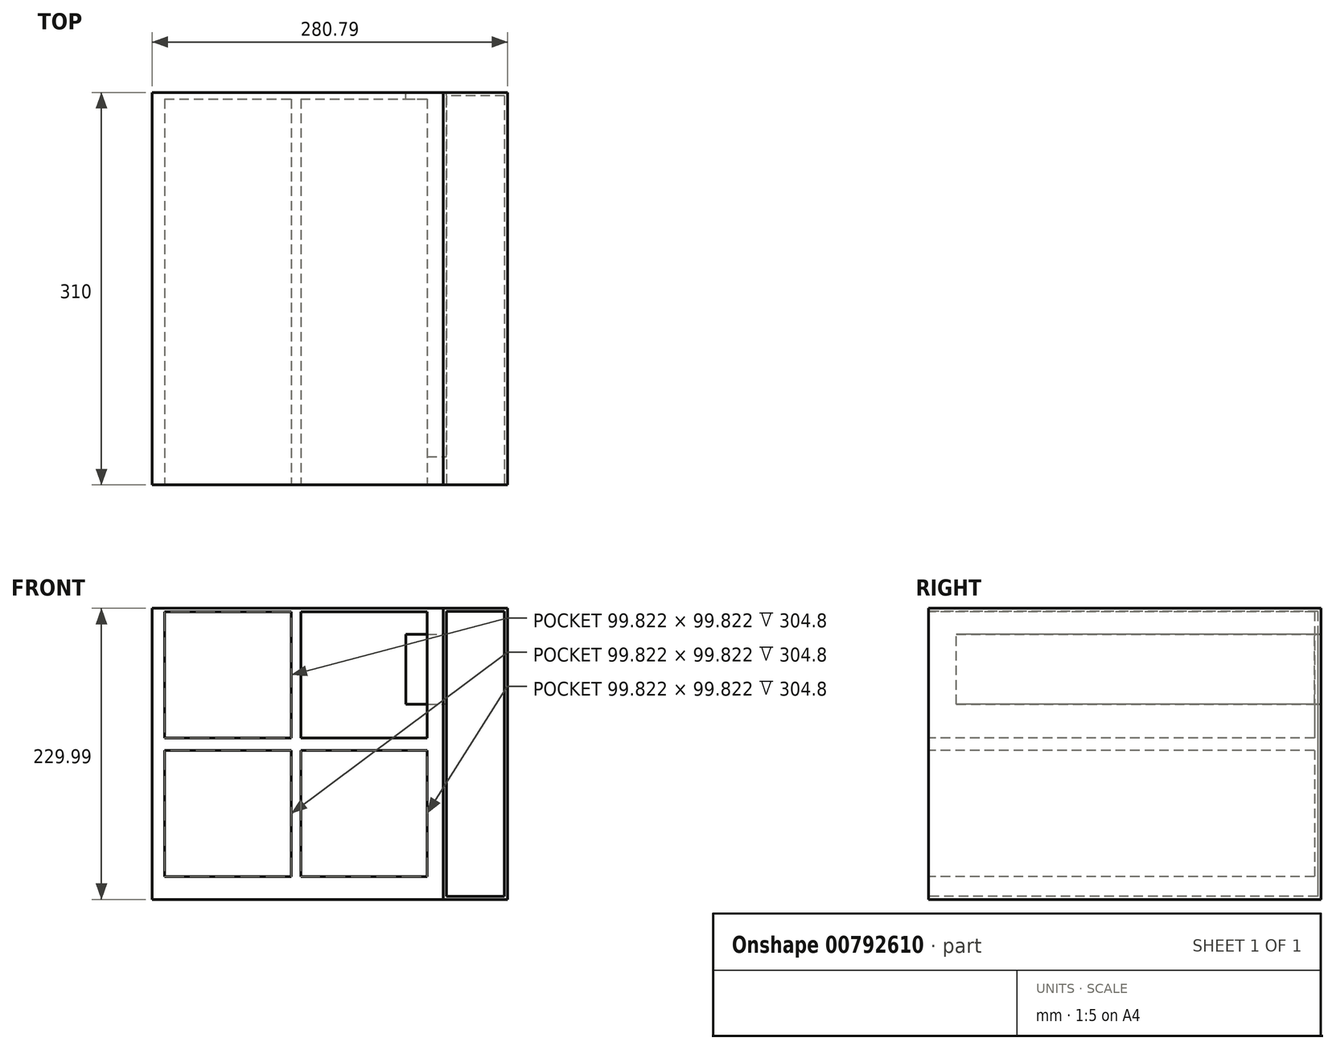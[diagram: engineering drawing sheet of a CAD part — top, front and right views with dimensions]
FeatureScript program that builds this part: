
annotation { "Feature Type Name" : "Feature", "Feature Type Description" : "" }
export const myFeature = defineFeature(function(context is Context, id is Id, definition is map)
    precondition{}
    {
        {
            var Q0;
            Q0=qCreatedBy(makeId("Front.planeOp"),FACE);
            var sketch = newSketch(context, id + "F0", { "sketchPlane" : qUnion([Q0])});
            skLineSegment(sketch, "E0.bottom", {"start": v(-110.85, 155.14) * mm, "end": v(119.14, 155.14) * mm});
            skLineSegment(sketch, "E0.top", {"start": v(-110.85, -74.85) * mm, "end": v(119.14, -74.85) * mm});
            skLineSegment(sketch, "E0.left", {"start": v(-110.85, 155.14) * mm, "end": v(-110.85, -74.85) * mm});
            skLineSegment(sketch, "E0.right", {"start": v(119.14, 155.14) * mm, "end": v(119.14, -74.85) * mm});
            skSolve(sketch);
        }
        {
            var Q0;
            Q0 = qSketchRegion(id + "F0", true);
            extrude(context, id + "F1", {"entities" : qUnion([Q0]), "oppositeDirection" : true, "depth" : 310 * mm, "offsetDistance" : 25.4 * mm});
        }
        {
            var Q0;
            Q0=makeQuery(id+"F1.opExtrude","CAP_FACE",FACE,{"disambiguationData":[OSD([sQuery(id+"F0.wireOp",EDGE,"E0.bottom"),sQuery(id+"F0.wireOp",EDGE,"E0.top"),sQuery(id+"F0.wireOp",EDGE,"E0.left"),sQuery(id+"F0.wireOp",EDGE,"E0.right")])],"isStart":true});
            var sketch = newSketch(context, id + "F2", { "sketchPlane" : qUnion([Q0])});
            skLineSegment(sketch, "E1", {"start": v(-110.85, 127.91) * mm, "end": v(-100.87, 127.91) * mm});
            skLineSegment(sketch, "E2.bottom", {"start": v(-100.87, 152.43) * mm, "end": v(-1.05, 152.43) * mm});
            skLineSegment(sketch, "E2.top", {"start": v(-100.87, 52.6) * mm, "end": v(-1.05, 52.6) * mm});
            skLineSegment(sketch, "E2.left", {"start": v(-100.87, 152.43) * mm, "end": v(-100.87, 52.6) * mm});
            skLineSegment(sketch, "E2.right", {"start": v(-1.05, 152.43) * mm, "end": v(-1.05, 52.6) * mm});
            skSolve(sketch);
        }
        {
            var Q0;
            {var subQ3=sQuery(id+"F2.wireOp",EDGE,"E2.bottom");Q0=makeQuery(id+"F2.imprint","IMPRINT",FACE,{"disambiguationData":[TD([[makeQuery(id+"F2.imprint","IMPRINT",EDGE,{"derivedFrom":subQ3}),-1.0]])]});}
            extrude(context, id + "F3", {"entities" : qUnion([Q0]), "operationType" : NewBodyOperationType.REMOVE, "oppositeDirection" : true, "depth" : 304.8 * mm, "offsetDistance" : 25.4 * mm});
        }
        {
            var Q0;
            Q0=makeQuery(id+"F1.opExtrude","CAP_FACE",FACE,{"disambiguationData":[OSD([sQuery(id+"F0.wireOp",EDGE,"E0.bottom"),sQuery(id+"F0.wireOp",EDGE,"E0.top"),sQuery(id+"F0.wireOp",EDGE,"E0.left"),sQuery(id+"F0.wireOp",EDGE,"E0.right")])],"isStart":true});
            var sketch = newSketch(context, id + "F4", { "sketchPlane" : qUnion([Q0])});
            skLineSegment(sketch, "E3.bottom", {"start": v(6.52, 152.43) * mm, "end": v(106.34, 152.43) * mm});
            skLineSegment(sketch, "E3.top", {"start": v(6.52, 52.6) * mm, "end": v(106.34, 52.6) * mm});
            skLineSegment(sketch, "E3.left", {"start": v(6.52, 152.43) * mm, "end": v(6.52, 52.6) * mm});
            skLineSegment(sketch, "E3.right", {"start": v(106.34, 152.43) * mm, "end": v(106.34, 52.6) * mm});
            skSolve(sketch);
        }
        {
            var Q0;
            Q0=makeQuery(id+"F4.imprint","IMPRINT",FACE,{"disambiguationData":[TD([[makeQuery(id+"F4.imprint","IMPRINT",EDGE,{"derivedFrom":sQuery(id+"F4.wireOp",EDGE,"E3.bottom")}),-1.0]])]});
            extrude(context, id + "F5", {"entities" : qUnion([Q0]), "operationType" : NewBodyOperationType.REMOVE, "oppositeDirection" : true, "depth" : 304.8 * mm, "offsetDistance" : 25.4 * mm});
        }
        {
            var Q0;
            Q0=makeQuery(id+"F1.opExtrude","CAP_FACE",FACE,{"disambiguationData":[OSD([sQuery(id+"F0.wireOp",EDGE,"E0.bottom"),sQuery(id+"F0.wireOp",EDGE,"E0.top"),sQuery(id+"F0.wireOp",EDGE,"E0.left"),sQuery(id+"F0.wireOp",EDGE,"E0.right")])],"isStart":true});
            var sketch = newSketch(context, id + "F6", { "sketchPlane" : qUnion([Q0])});
            skLineSegment(sketch, "E4.bottom", {"start": v(-100.87, 42.92) * mm, "end": v(-1.05, 42.92) * mm});
            skLineSegment(sketch, "E4.top", {"start": v(-100.87, -56.9) * mm, "end": v(-1.05, -56.9) * mm});
            skLineSegment(sketch, "E4.left", {"start": v(-100.87, 42.92) * mm, "end": v(-100.87, -56.9) * mm});
            skLineSegment(sketch, "E4.right", {"start": v(-1.05, 42.92) * mm, "end": v(-1.05, -56.9) * mm});
            skSolve(sketch);
        }
        {
            var Q0;
            Q0 = qSketchRegion(id + "F6", true);
            extrude(context, id + "F7", {"entities" : qUnion([Q0]), "operationType" : NewBodyOperationType.REMOVE, "oppositeDirection" : true, "depth" : 304.8 * mm, "offsetDistance" : 25.4 * mm});
        }
        {
            var Q0;
            Q0=makeQuery(id+"F1.opExtrude","CAP_FACE",FACE,{"disambiguationData":[OSD([sQuery(id+"F0.wireOp",EDGE,"E0.bottom"),sQuery(id+"F0.wireOp",EDGE,"E0.top"),sQuery(id+"F0.wireOp",EDGE,"E0.left"),sQuery(id+"F0.wireOp",EDGE,"E0.right")])],"isStart":true});
            var sketch = newSketch(context, id + "F8", { "sketchPlane" : qUnion([Q0])});
            skLineSegment(sketch, "E5.bottom", {"start": v(6.52, 42.92) * mm, "end": v(106.34, 42.92) * mm});
            skLineSegment(sketch, "E5.top", {"start": v(6.52, -56.9) * mm, "end": v(106.34, -56.9) * mm});
            skLineSegment(sketch, "E5.left", {"start": v(6.52, 42.92) * mm, "end": v(6.52, -56.9) * mm});
            skLineSegment(sketch, "E5.right", {"start": v(106.34, 42.92) * mm, "end": v(106.34, -56.9) * mm});
            skSolve(sketch);
        }
        {
            var Q0;
            Q0 = qSketchRegion(id + "F8", true);
            extrude(context, id + "F9", {"entities" : qUnion([Q0]), "operationType" : NewBodyOperationType.REMOVE, "oppositeDirection" : true, "depth" : 304.8 * mm, "offsetDistance" : 25.4 * mm});
        }
        {
            var Q0;
            Q0=makeQuery(id+"F1.opExtrude","SWEPT_FACE",FACE,{"disambiguationData":[OSD([sQuery(id+"F0.wireOp",EDGE,"E0.right")])]});
            extrude(context, id + "F10", {"entities" : qUnion([Q0]), "depth" : 50.8 * mm, "offsetDistance" : 25.4 * mm});
        }
        {
            var Q0;
            {var subQ0=sQuery(id+"F0.wireOp",EDGE,"E0.right");Q0=makeQuery(id+"F10.opExtrude","SWEPT_FACE",FACE,{"disambiguationData":[OSD([subQ0]),TDD([makeQuery(id+"F1.opExtrude","CAP_EDGE",EDGE,{"disambiguationData":[OSD([subQ0])],"isStart":true})])]});}
            shell(context, id + "F11", {"entities" : qUnion([Q0]), "thickness" : 2.54 * mm});
        }
        {
            var Q0;
            {var subQ0=sQuery(id+"F0.wireOp",EDGE,"E0.right");Q0=makeQuery(id+"F11.opShell","OFFSET_FACE",FACE,{"disambiguationData":[OSD([subQ0]),TDD([makeQuery(id+"F10.opExtrude","CAP_FACE",FACE,{"disambiguationData":[OSD([subQ0])],"isStart":true})])]});}
            var sketch = newSketch(context, id + "F12", { "sketchPlane" : qUnion([Q0])});
            skLineSegment(sketch, "E6.bottom", {"start": v(22.17, 134.66) * mm, "end": v(363.62, 134.66) * mm});
            skLineSegment(sketch, "E6.top", {"start": v(22.17, 79.35) * mm, "end": v(363.62, 79.35) * mm});
            skLineSegment(sketch, "E6.left", {"start": v(22.17, 134.66) * mm, "end": v(22.17, 79.35) * mm});
            skLineSegment(sketch, "E6.right", {"start": v(363.62, 134.66) * mm, "end": v(363.62, 79.35) * mm});
            skSolve(sketch);
        }
        {
            var Q0;
            Q0 = qSketchRegion(id + "F12", true);
            extrude(context, id + "F13", {"entities" : qUnion([Q0]), "operationType" : NewBodyOperationType.REMOVE, "oppositeDirection" : true, "depth" : 32.26 * mm, "offsetDistance" : 25.4 * mm});
        }
        {
            var Q0;
            Q0=makeQuery(id+"F1.opExtrude","SWEPT_FACE",FACE,{"disambiguationData":[OSD([sQuery(id+"F0.wireOp",EDGE,"E0.right")])]});
            var sketch = newSketch(context, id + "F14", { "sketchPlane" : qUnion([Q0])});
            skLineSegment(sketch, "E7.bottom", {"start": v(25.96, 134.24) * mm, "end": v(310, 134.24) * mm});
            skLineSegment(sketch, "E7.top", {"start": v(25.96, 80.01) * mm, "end": v(310, 80.01) * mm});
            skLineSegment(sketch, "E7.left", {"start": v(25.96, 134.24) * mm, "end": v(25.96, 80.01) * mm});
            skLineSegment(sketch, "E7.right", {"start": v(310, 134.24) * mm, "end": v(310, 80.01) * mm});
            skSolve(sketch);
        }
        {
            var Q0;
            Q0 = qSketchRegion(id + "F14", true);
            extrude(context, id + "F15", {"entities" : qUnion([Q0]), "operationType" : NewBodyOperationType.REMOVE, "oppositeDirection" : true, "depth" : 25.9 * mm, "offsetDistance" : 25.4 * mm});
        }
    });
